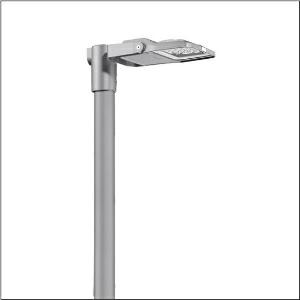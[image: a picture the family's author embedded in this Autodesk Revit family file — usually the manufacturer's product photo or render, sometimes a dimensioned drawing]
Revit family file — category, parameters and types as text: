
# Revit family: floodlight_fl_21_iq_micro___pl33t_5xa7761a2f3a_d57c
name_source: partatom
category: Lighting Fixtures
units: mm (PartAtom-declared; Revit-internal decimal feet)

## family parameters
Cut with Voids When Loaded = No
Host = Face
Light Source = No
Part Type = Normal
Room Calculation Point = No
Round Connector Dimension = Use Diameter
Shared = No

## types (1)
- --- (1 x LED, 2930 lm, 23.1 W, 3000K)
    Apparent Load = 23 VA
    CIE Flux Codes = 26 75 99 100 100
    Color Rendering = 70
    Color Temperature = 3000K
    Default Elevation = 1800 mm
    Description = Floodlight FL 21 iQ micro, floodlight, primary light control with lens, of PMMA, primary optical cover: protective disc, of toughened safety glass, transparent, light distribution: PL33T, light emission: direct distribution, installation type: surface-mounted, LED, High Power LED, rated luminous flux: 2.930lm, luminous efficacy: 127lm/W, light colour: 730, colour temperature: 3000K, control: optimised constant luminous flux control (CLO 2.0), Desk-Remote (wireless, voltage-free reading and setting of iQ features in the workshop via application-optimized NFC function/RFID function), Light-Fading, Smart-Wire, Night-Set, Lumen-Switch, Temp-Guard, Auto-Match, with terminal, 6-pole, mains connection: 220..240V, AC, 50/60Hz, start of lifetime: 23W, end of service life: 24W, reduction: 11W, luminaire housing, of diecast aluminium, powder-coated, Siteco® metallic grey (DB 702S), corrosivity category C5 mid according to DIN EN ISO 12944, sealing non-destructively replaceable, please order mast flange separately, mast bracket, of steel, galvanised, powder-coated, Siteco® metallic grey (DB 702S), protection rating (complete): IP66, insulation class (complete): insulation class II (safety insulation), certification: CE, ENEC, VDE, protection symbol: D, impact resistance: IK07, permissible operating ambient temperature: -40..+40°C, permissible operating ambient temperature for outdoor applications: -40..+50°C, standard: DIN EN 12944, LABS conformity tested according to VDMA 24364:2018-05, packaging unit: 1 piece

Light Distribution: PL33T
    Height = 65 mm
    Lamp = 1 x LED
    Lamp Light Flux = 2930 lm
    Lamp Power = 23.1 W
    Lamp count = 1
    Length = 312 mm
    Luminous efficacy = 127 lm/W
    Manufacturer = Siteco
    ModVariant = No
    Model = 5XA7761A2F3A
    Number of Poles = 1
    OnlyDefault = Yes
    Power Factor = 1
    Product Name = Floodlight FL 21 iQ micro | PL33T
    Product group = floodlight | pylon top
    ProductGroupID = 6101
    Protection Class = Protection class II
    Protection Degree = IP 66
    RLX_Detail_Level = 1
    RLX_Emergency_Light_Flux = 0 lm
    RLX_Emergency_Type = 0
    RLX_Emergency_Type_DB = No
    RlxData = <blob elided: 101637 chars, md5=2a2f4d67>
    Socket = socket
    Standby Power = 0 W
    System Light Flux = 2930 lm
    System Power = 23 W
    Type Comments = factory setting: luminous flux: 100 % | dim-lin: 254 | 455 mA
    Type Image = l_1007121.jpg
    URL = http://relux.com
    VarID = @adj_098383
    Voltage = 0 V
    Weight = 0.00 kg
    Width = 230 mm

## geometry (parser evidence)
native form markers: Blend x4, Sweep x13
no freeform markers — native parametric forms only
